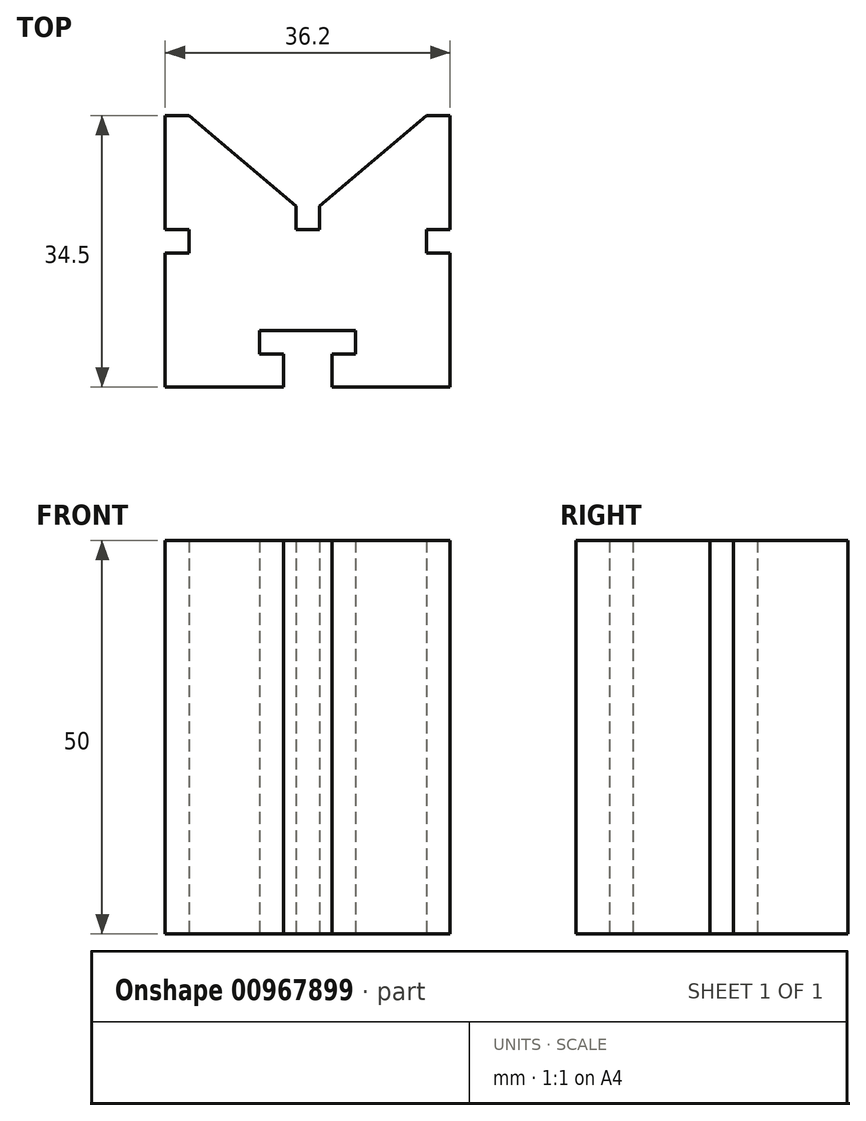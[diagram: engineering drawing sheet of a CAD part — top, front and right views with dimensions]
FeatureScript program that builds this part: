
annotation { "Feature Type Name" : "Feature", "Feature Type Description" : "" }
export const myFeature = defineFeature(function(context is Context, id is Id, definition is map)
    precondition{}
    {
        {
            var Q0;
            Q0=qCreatedBy(makeId("Top.planeOp"),FACE);
            var sketch = newSketch(context, id + "F0", { "sketchPlane" : qUnion([Q0])});
            skLineSegment(sketch, "E0.bottom", {"start": v(18.1, 17.25) * mm, "end": v(15.1, 17.25) * mm});
            skLineSegment(sketch, "E0.top", {"start": v(18.1, -17.25) * mm, "end": v(-18.1, -17.25) * mm});
            skLineSegment(sketch, "E0.left", {"start": v(18.1, 17.25) * mm, "end": v(18.1, -17.25) * mm});
            skLineSegment(sketch, "E0.right", {"start": v(-18.1, 17.25) * mm, "end": v(-18.1, -17.25) * mm});
            skPoint(sketch, "E0.middle", {"position": v(0, 0) * mm});
            skLineSegment(sketch, "E1", {"start": v(-15.1, 17.25) * mm, "end": v(-1.48, 5.75) * mm});
            skLineSegment(sketch, "E2", {"start": v(-1.48, 5.75) * mm, "end": v(-1.48, 2.75) * mm});
            skLineSegment(sketch, "E3", {"start": v(-1.48, 2.75) * mm, "end": v(1.52, 2.75) * mm});
            skLineSegment(sketch, "E4", {"start": v(1.52, 2.75) * mm, "end": v(1.52, 5.75) * mm});
            skLineSegment(sketch, "E5", {"start": v(1.52, 5.75) * mm, "end": v(15.1, 17.25) * mm});
            skLineSegment(sketch, "E6.trimOffspring", {"start": v(-15.1, 17.25) * mm, "end": v(-18.1, 17.25) * mm});
            skSolve(sketch);
        }
        {
            var Q0;
            Q0 = qSketchRegion(id + "F0", true);
            extrude(context, id + "F1", {"entities" : qUnion([Q0]), "depth" : 50 * mm, "offsetDistance" : 25 * mm});
        }
        {
            var Q0;
            Q0=qCreatedBy(makeId("Top.planeOp"),FACE);
            var sketch = newSketch(context, id + "F2", { "sketchPlane" : qUnion([Q0])});
            skLineSegment(sketch, "E7", {"start": v(-6.1, -10.05) * mm, "end": v(-6.1, -13.05) * mm});
            skLineSegment(sketch, "E8", {"start": v(-6.1, -13.05) * mm, "end": v(-3.1, -13.05) * mm});
            skLineSegment(sketch, "E9", {"start": v(-3.1, -13.05) * mm, "end": v(-3.1, -21.21) * mm});
            skLineSegment(sketch, "E10", {"start": v(-3.1, -21.21) * mm, "end": v(3.1, -21.21) * mm});
            skLineSegment(sketch, "E11", {"start": v(3.1, -21.21) * mm, "end": v(3.1, -13.05) * mm});
            skLineSegment(sketch, "E12", {"start": v(3.1, -13.05) * mm, "end": v(6.1, -13.05) * mm});
            skLineSegment(sketch, "E13", {"start": v(-6.1, -10.05) * mm, "end": v(6.1, -10.05) * mm});
            skLineSegment(sketch, "E14", {"start": v(6.1, -10.05) * mm, "end": v(6.1, -13.05) * mm});
            skSolve(sketch);
        }
        {
            var Q0;
            Q0 = qSketchRegion(id + "F2", true);
            extrude(context, id + "F3", {"entities" : qUnion([Q0]), "operationType" : NewBodyOperationType.REMOVE, "oppositeDirection" : true, "depth" : -50 * mm, "offsetDistance" : 25 * mm});
        }
        {
            var Q0;
            Q0=qCreatedBy(makeId("Top.planeOp"),FACE);
            var sketch = newSketch(context, id + "F4", { "sketchPlane" : qUnion([Q0])});
            skLineSegment(sketch, "E15", {"start": v(-18.78, 2.75) * mm, "end": v(-15.1, 2.75) * mm});
            skLineSegment(sketch, "E16", {"start": v(-15.1, 2.75) * mm, "end": v(-15.1, -0.25) * mm});
            skLineSegment(sketch, "E17", {"start": v(-15.1, -0.25) * mm, "end": v(-18.78, -0.25) * mm});
            skLineSegment(sketch, "E18", {"start": v(-18.78, -0.25) * mm, "end": v(-18.78, 2.75) * mm});
            skLineSegment(sketch, "E19", {"start": v(15.1, 2.75) * mm, "end": v(15.1, -0.25) * mm});
            skPoint(sketch, "E19.startSnap0", {"position": v(-16.94, 2.75) * mm});
            skLineSegment(sketch, "E20", {"start": v(15.1, -0.25) * mm, "end": v(21.5, -0.25) * mm});
            skLineSegment(sketch, "E21", {"start": v(15.1, 2.75) * mm, "end": v(21.5, 2.75) * mm});
            skLineSegment(sketch, "E22", {"start": v(21.5, 2.75) * mm, "end": v(21.5, -0.25) * mm});
            skSolve(sketch);
        }
        {
            var Q0;
            Q0=makeQuery(id+"F4.imprint","IMPRINT",FACE,{"disambiguationData":[TD([[makeQuery(id+"F4.imprint","IMPRINT",EDGE,{"derivedFrom":sQuery(id+"F4.wireOp",EDGE,"E15")}),-1.0]])]});
            var Q1;
            Q1=makeQuery(id+"F4.imprint","IMPRINT",FACE,{"disambiguationData":[TD([[makeQuery(id+"F4.imprint","IMPRINT",EDGE,{"derivedFrom":sQuery(id+"F4.wireOp",EDGE,"E19")}),1.0]])]});
            extrude(context, id + "F5", {"entities" : qUnion([Q0, Q1]), "operationType" : NewBodyOperationType.REMOVE, "oppositeDirection" : true, "depth" : -50 * mm, "offsetDistance" : 25 * mm});
        }
    });
